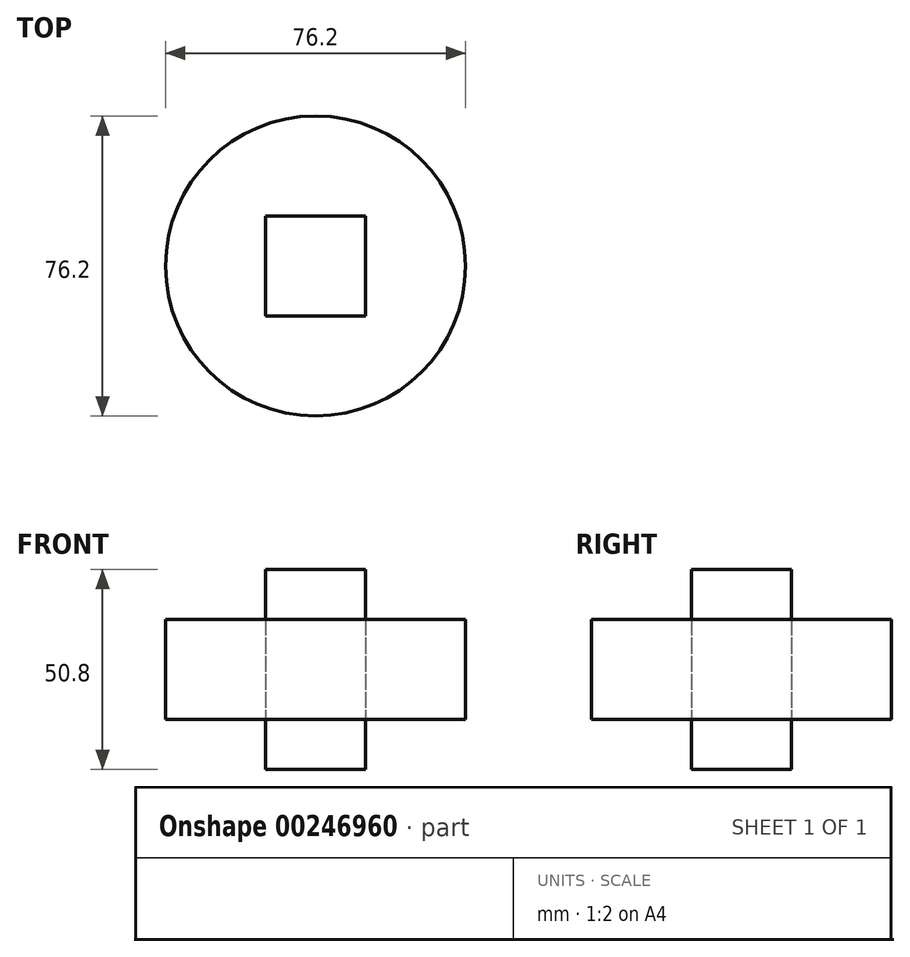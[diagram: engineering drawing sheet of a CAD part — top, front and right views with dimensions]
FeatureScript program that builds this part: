
annotation { "Feature Type Name" : "Feature", "Feature Type Description" : "" }
export const myFeature = defineFeature(function(context is Context, id is Id, definition is map)
    precondition{}
    {
        {
            var Q0;
            Q0=qCreatedBy(makeId("Top.planeOp"),FACE);
            var sketch = newSketch(context, id + "F0", { "sketchPlane" : qUnion([Q0])});
            skCircle(sketch, "E0", {"center": v(0, 0) * mm, "radius": 38.1 * mm});
            skSolve(sketch);
        }
        {
            var Q0;
            Q0 = qSketchRegion(id + "F0", true);
            extrude(context, id + "F1", {"entities" : qUnion([Q0]), "endBound" : BoundingType.SYMMETRIC, "depth" : 25.4 * mm});
        }
        {
            var Q0;
            Q0=qCreatedBy(makeId("Top.planeOp"),FACE);
            var sketch = newSketch(context, id + "F2", { "sketchPlane" : qUnion([Q0])});
            skLineSegment(sketch, "E1.bottom", {"start": v(12.7, -12.7) * mm, "end": v(-12.7, -12.7) * mm});
            skLineSegment(sketch, "E1.top", {"start": v(12.7, 12.7) * mm, "end": v(-12.7, 12.7) * mm});
            skLineSegment(sketch, "E1.left", {"start": v(12.7, -12.7) * mm, "end": v(12.7, 12.7) * mm});
            skLineSegment(sketch, "E1.right", {"start": v(-12.7, -12.7) * mm, "end": v(-12.7, 12.7) * mm});
            skPoint(sketch, "E1.middle", {"position": v(0, 0) * mm});
            skSolve(sketch);
        }
        {
            var Q0;
            Q0 = qSketchRegion(id + "F2", true);
            extrude(context, id + "F3", {"entities" : qUnion([Q0]), "endBound" : BoundingType.SYMMETRIC, "depth" : 50.8 * mm});
        }
        {
            var Q0;
            Q0=makeQuery(id+"F3.opExtrude","SWEPT_BODY",BODY,{"disambiguationData":[OSD([sQuery(id+"F2.wireOp",EDGE,"E1.bottom"),sQuery(id+"F2.wireOp",EDGE,"E1.top"),sQuery(id+"F2.wireOp",EDGE,"E1.left"),sQuery(id+"F2.wireOp",EDGE,"E1.right")])]});
            var Q1;
            Q1=makeQuery(id+"F1.opExtrude","SWEPT_BODY",BODY,{"disambiguationData":[OSD([sQuery(id+"F0.wireOp",EDGE,"E0")])]});
            booleanBodies(context, id + "F4", {"operationType" : BooleanOperationType.INTERSECTION, "tools" : qUnion([Q0, Q1]), "keepTools" : true});
        }
    });
